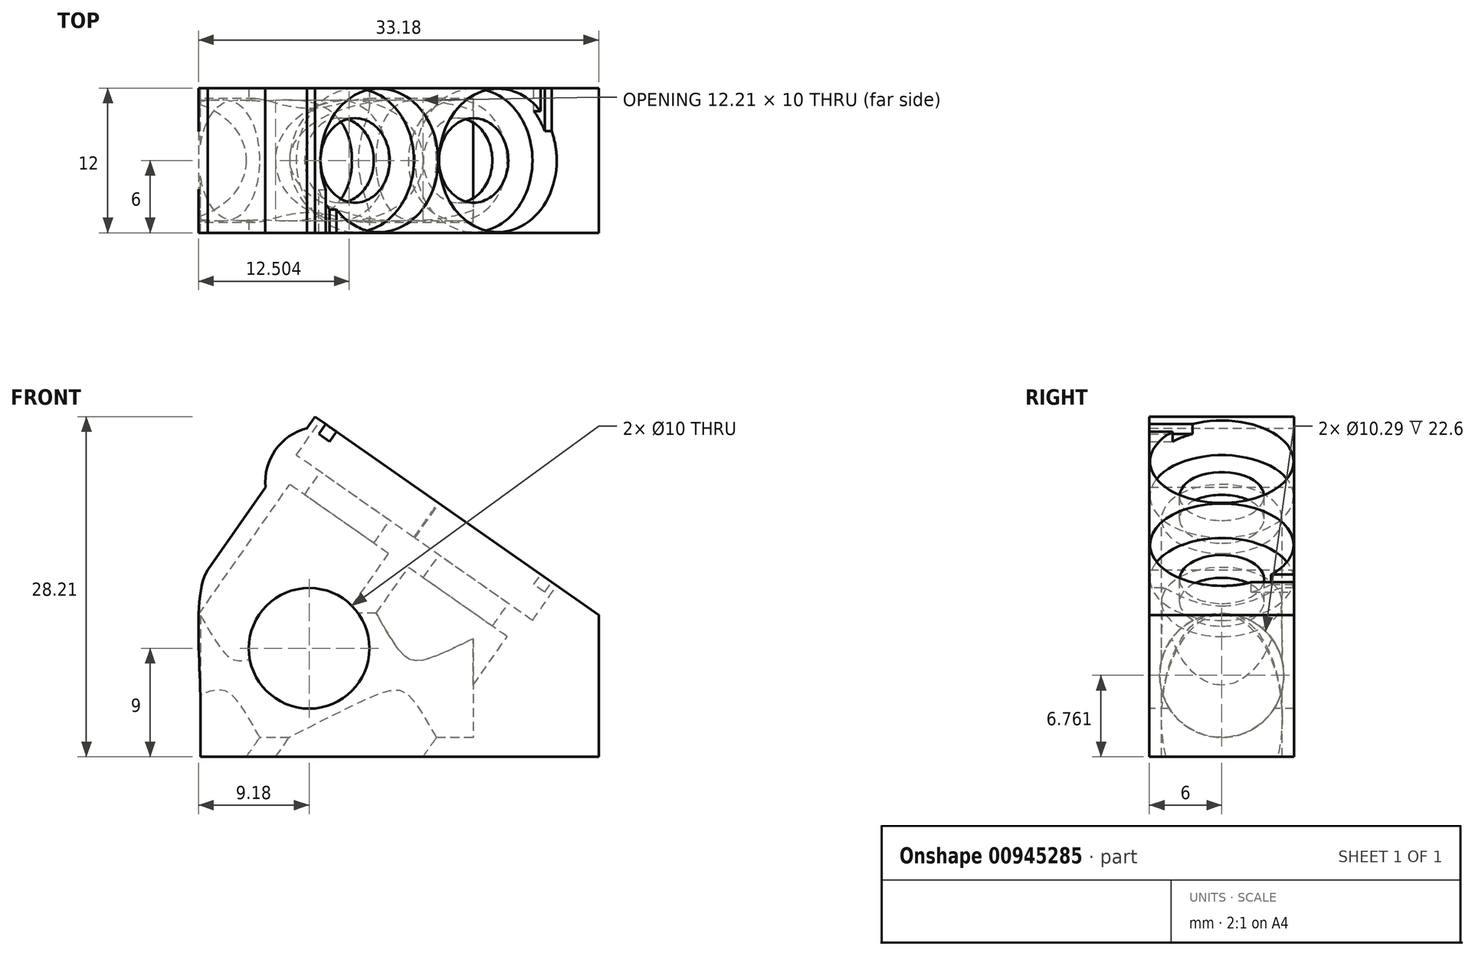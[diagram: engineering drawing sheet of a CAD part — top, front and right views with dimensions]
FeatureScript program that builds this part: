
annotation { "Feature Type Name" : "Feature", "Feature Type Description" : "" }
export const myFeature = defineFeature(function(context is Context, id is Id, definition is map)
    precondition{}
    {
        {
            var Q0;
            Q0=qCreatedBy(makeId("Front.planeOp"),FACE);
            var sketch = newSketch(context, id + "F0", { "sketchPlane" : qUnion([Q0])});
            skLineSegment(sketch, "E0.bottom", {"start": v(0, 0) * mm, "end": v(-33, 0) * mm});
            skLineSegment(sketch, "E0.top", {"start": v(0, 4) * mm, "end": v(-33, 4) * mm});
            skLineSegment(sketch, "E0.left", {"start": v(0, 0) * mm, "end": v(0, 4) * mm});
            skLineSegment(sketch, "E0.right", {"start": v(-33, 0) * mm, "end": v(-33, 4) * mm});
            skLineSegment(sketch, "E1", {"start": v(-30.88, 15.06) * mm, "end": v(-9.83, 0.32) * mm, "construction": true});
            skLineSegment(sketch, "E2", {"start": v(-9.83, 0.32) * mm, "end": v(-1.23, 12.6) * mm, "construction": true});
            skLineSegment(sketch, "E3", {"start": v(-1.23, 12.6) * mm, "end": v(0, 11.74) * mm, "construction": true});
            skLineSegment(sketch, "E4", {"start": v(-22.28, 27.35) * mm, "end": v(-30.88, 15.06) * mm, "construction": true});
            skLineSegment(sketch, "E5", {"start": v(0, 4) * mm, "end": v(0, 11.74) * mm});
            skLineSegment(sketch, "E6", {"start": v(-32.4, 15.5) * mm, "end": v(-15.96, 4) * mm});
            skLineSegment(sketch, "E7", {"start": v(0, 7.87) * mm, "end": v(13.32, 7.87) * mm});
            skLineSegment(sketch, "E8", {"start": v(13.32, 7.87) * mm, "end": v(13.32, 0) * mm});
            skLineSegment(sketch, "E9", {"start": v(13.32, 0) * mm, "end": v(0, 0) * mm});
            skLineSegment(sketch, "E10", {"start": v(21.82, 30.5) * mm, "end": v(-34.66, 30.5) * mm, "construction": true});
            skLineSegment(sketch, "E11", {"start": v(-22.28, 27.35) * mm, "end": v(-23.5, 28.2) * mm, "construction": true});
            skLineSegment(sketch, "E12", {"start": v(-23.5, 28.2) * mm, "end": v(-21.9, 30.5) * mm, "construction": true});
            skLineSegment(sketch, "E13", {"start": v(-21.9, 30.5) * mm, "end": v(1.6, 14.04) * mm, "construction": true});
            skLineSegment(sketch, "E14", {"start": v(0, 11.74) * mm, "end": v(1.6, 14.04) * mm, "construction": true});
            skLineSegment(sketch, "E15", {"start": v(-29.2, 13.88) * mm, "end": v(-31.73, 10.28) * mm, "construction": true});
            skLineSegment(sketch, "E16", {"start": v(-31.73, 10.28) * mm, "end": v(-14.04, -2.11) * mm, "construction": true});
            skLineSegment(sketch, "E17", {"start": v(-14.04, -2.11) * mm, "end": v(-11.51, 1.5) * mm, "construction": true});
            skLineSegment(sketch, "E18", {"start": v(-22.88, 4.08) * mm, "end": v(-20.36, 7.69) * mm, "construction": true});
            skLineSegment(sketch, "E19", {"start": v(0, 11.74) * mm, "end": v(-23.5, 28.2) * mm});
            skLineSegment(sketch, "E20", {"start": v(-23.5, 28.2) * mm, "end": v(-32.4, 15.5) * mm});
            skLineSegment(sketch, "E21", {"start": v(-1.1, 12.52) * mm, "end": v(-9.87, 0) * mm});
            skLineSegment(sketch, "E22", {"start": v(-22.4, 27.43) * mm, "end": v(-31.3, 14.74) * mm});
            skFitSpline(sketch, "E23", {"points": [v(-32.4, 15.5) * mm, v(-33, 4) * mm], "startDerivative": vector(-3.84, -5.87) * mm, "endDerivative": vector(0, -11.95) * mm});
            skLineSegment(sketch, "E24", {"start": v(-15.96, 4) * mm, "end": v(-10.25, 0) * mm});
            skLineSegment(sketch, "E25", {"start": v(-23.03, 26.54) * mm, "end": v(-25.92, 24.77) * mm});
            skLineSegment(sketch, "E26", {"start": v(-25.92, 24.77) * mm, "end": v(-26.47, 21.62) * mm});
            skLineSegment(sketch, "E27.MirrorCS", {"start": v(-1.73, 11.62) * mm, "end": v(-2.4, 8.3) * mm});
            skLineSegment(sketch, "E28.MirrorCS", {"start": v(-2.4, 8.3) * mm, "end": v(-5.17, 6.7) * mm});
            skArc(sketch, "E29", {"start": v(-24.18, 27.25) * mm, "mid": v(-26.8, 25.44) * mm, "end": v(-27.6, 22.35) * mm});
            skLineSegment(sketch, "E30", {"start": v(-23.25, 28.02) * mm, "end": v(-25.23, 25.19) * mm});
            skLineSegment(sketch, "E31.MirrorCS", {"start": v(-0.26, 11.93) * mm, "end": v(-2.25, 9.1) * mm});
            skSolve(sketch);
        }
        {
            var Q0;
            {var subQ0=sQuery(id+"F0.wireOp",EDGE,"E21");var subQ1=sQuery(id+"F0.wireOp",EDGE,"E19");var subQ2=makeQuery(id+"F0.imprint","INTERSECT",VERTEX,{"derivedFrom":[subQ1,subQ0]});Q0=makeQuery(id+"F0.imprint","IMPRINT",FACE,{"disambiguationData":[TD([[makeQuery(id+"F0.imprint","IMPRINT",EDGE,{"disambiguationData":[TD([[subQ2,-1.0]])],"derivedFrom":subQ1}),1.0]])]});}
            var Q1;
            {var subQ3=sQuery(id+"F0.wireOp",EDGE,"E26");Q1=makeQuery(id+"F0.imprint","IMPRINT",FACE,{"disambiguationData":[TD([[makeQuery(id+"F0.imprint","IMPRINT",EDGE,{"derivedFrom":subQ3}),1.0]])]});}
            var Q2;
            {var subQ4=sQuery(id+"F0.wireOp",EDGE,"E26");Q2=makeQuery(id+"F0.imprint","IMPRINT",FACE,{"disambiguationData":[TD([[makeQuery(id+"F0.imprint","IMPRINT",EDGE,{"derivedFrom":subQ4}),-1.0]])]});}
            var Q3;
            {var subQ2=sQuery(id+"F0.wireOp",EDGE,"E29");Q3=makeQuery(id+"F0.imprint","IMPRINT",FACE,{"disambiguationData":[TD([[makeQuery(id+"F0.imprint","IMPRINT",EDGE,{"derivedFrom":subQ2}),1.0]])]});}
            var Q4;
            {var subQ3=sQuery(id+"F0.wireOp",EDGE,"E30");Q4=makeQuery(id+"F0.imprint","IMPRINT",FACE,{"disambiguationData":[TD([[makeQuery(id+"F0.imprint","IMPRINT",EDGE,{"derivedFrom":subQ3}),1.0]])]});}
            var Q5;
            {var subQ6=sQuery(id+"F0.wireOp",EDGE,"E30");Q5=makeQuery(id+"F0.imprint","IMPRINT",FACE,{"disambiguationData":[TD([[makeQuery(id+"F0.imprint","IMPRINT",EDGE,{"derivedFrom":subQ6}),-1.0]])]});}
            var Q6;
            {var subQ0=sQuery(id+"F0.wireOp",EDGE,"E23");Q6=makeQuery(id+"F0.imprint","IMPRINT",FACE,{"disambiguationData":[TD([[makeQuery(id+"F0.imprint","IMPRINT",EDGE,{"derivedFrom":subQ0}),1.0]])]});}
            var Q7;
            {var subQ0=sQuery(id+"F0.wireOp",EDGE,"E0.right");Q7=makeQuery(id+"F0.imprint","IMPRINT",FACE,{"disambiguationData":[TD([[makeQuery(id+"F0.imprint","IMPRINT",EDGE,{"derivedFrom":subQ0}),-1.0]])]});}
            var Q8;
            {var subQ3=sQuery(id+"F0.wireOp",EDGE,"E24");Q8=makeQuery(id+"F0.imprint","IMPRINT",FACE,{"disambiguationData":[TD([[makeQuery(id+"F0.imprint","IMPRINT",EDGE,{"derivedFrom":subQ3}),1.0]])]});}
            var Q9;
            {var subQ0=sQuery(id+"F0.wireOp",EDGE,"E0.left");Q9=makeQuery(id+"F0.imprint","IMPRINT",FACE,{"disambiguationData":[TD([[makeQuery(id+"F0.imprint","IMPRINT",EDGE,{"derivedFrom":subQ0}),1.0]])]});}
            var Q10;
            {var subQ4=sQuery(id+"F0.wireOp",EDGE,"E28.MirrorCS");Q10=makeQuery(id+"F0.imprint","IMPRINT",FACE,{"disambiguationData":[TD([[makeQuery(id+"F0.imprint","IMPRINT",EDGE,{"derivedFrom":subQ4}),1.0]])]});}
            var Q11;
            {var subQ3=sQuery(id+"F0.wireOp",EDGE,"E28.MirrorCS");Q11=makeQuery(id+"F0.imprint","IMPRINT",FACE,{"disambiguationData":[TD([[makeQuery(id+"F0.imprint","IMPRINT",EDGE,{"derivedFrom":subQ3}),-1.0]])]});}
            var Q12;
            {var subQ3=sQuery(id+"F0.wireOp",EDGE,"E31.MirrorCS");Q12=makeQuery(id+"F0.imprint","IMPRINT",FACE,{"disambiguationData":[TD([[makeQuery(id+"F0.imprint","IMPRINT",EDGE,{"derivedFrom":subQ3}),-1.0]])]});}
            extrude(context, id + "F1", {"entities" : qUnion([Q0, Q1, Q2, Q3, Q4, Q5, Q6, Q7, Q8, Q9, Q10, Q11, Q12]), "endBound" : BoundingType.SYMMETRIC, "depth" : 12 * mm, "offsetDistance" : 25 * mm});
        }
        {
            var Q0;
            Q0=makeQuery(id+"F1.opExtrude","CAP_FACE",FACE,{"disambiguationData":[OSD([sQuery(id+"F0.wireOp",EDGE,"E0.bottom"),sQuery(id+"F0.wireOp",EDGE,"E0.left"),sQuery(id+"F0.wireOp",EDGE,"E0.right"),sQuery(id+"F0.wireOp",EDGE,"E5"),sQuery(id+"F0.wireOp",EDGE,"E19"),sQuery(id+"F0.wireOp",EDGE,"E20"),sQuery(id+"F0.wireOp",EDGE,"E23"),sQuery(id+"F0.wireOp",EDGE,"E29")])],"isStart":false});
            var sketch = newSketch(context, id + "F2", { "sketchPlane" : qUnion([Q0])});
            skCircle(sketch, "E32", {"center": v(-24, 9) * mm, "radius": 5 * mm});
            skSolve(sketch);
        }
        {
            var Q0;
            Q0=makeQuery(id+"F2.imprint","IMPRINT",FACE,{"disambiguationData":[TD([[makeQuery(id+"F2.imprint","IMPRINT",EDGE,{"derivedFrom":sQuery(id+"F2.wireOp",EDGE,"E32")}),1.0]])]});
            extrude(context, id + "F3", {"entities" : qUnion([Q0]), "operationType" : NewBodyOperationType.REMOVE, "oppositeDirection" : true, "depth" : 25 * mm, "offsetDistance" : 25 * mm});
        }
        {
            var Q0;
            Q0=makeQuery(id+"F1.opExtrude","SWEPT_FACE",FACE,{"disambiguationData":[OSD([sQuery(id+"F0.wireOp",EDGE,"E19")])]});
            var sketch = newSketch(context, id + "F4", { "sketchPlane" : qUnion([Q0])});
            skCircle(sketch, "E33", {"center": v(-28.94, 0) * mm, "radius": 3.5 * mm});
            skCircle(sketch, "E34", {"center": v(-16.94, 0) * mm, "radius": 3.5 * mm});
            skCircle(sketch, "E35", {"center": v(-28.94, 0) * mm, "radius": 5 * mm});
            skCircle(sketch, "E36", {"center": v(-16.94, 0) * mm, "radius": 5 * mm});
            skCircle(sketch, "E37", {"center": v(-28.94, 0) * mm, "radius": 5.95 * mm});
            skCircle(sketch, "E38", {"center": v(-16.94, 0) * mm, "radius": 5.95 * mm});
            skLineSegment(sketch, "E39", {"start": v(-34.37, -6) * mm, "end": v(-34.37, -2.43) * mm});
            skLineSegment(sketch, "E40", {"start": v(-33.27, -6) * mm, "end": v(-33.27, -4.08) * mm});
            skLineSegment(sketch, "E41", {"start": v(-12.6, 4.08) * mm, "end": v(-12.6, 6) * mm});
            skLineSegment(sketch, "E42", {"start": v(-11.5, 2.43) * mm, "end": v(-11.5, 6) * mm});
            skSolve(sketch);
        }
        {
            var Q0;
            Q0=makeQuery(id+"F4.imprint","IMPRINT",FACE,{"disambiguationData":[TD([[makeQuery(id+"F4.imprint","IMPRINT",EDGE,{"derivedFrom":sQuery(id+"F4.wireOp",EDGE,"E33")}),-1.0]])]});
            var Q1;
            Q1=makeQuery(id+"F4.imprint","IMPRINT",FACE,{"disambiguationData":[TD([[makeQuery(id+"F4.imprint","IMPRINT",EDGE,{"derivedFrom":sQuery(id+"F4.wireOp",EDGE,"E34")}),-1.0]])]});
            extrude(context, id + "F5", {"entities" : qUnion([Q0, Q1]), "operationType" : NewBodyOperationType.REMOVE, "oppositeDirection" : true, "depth" : 32.3 * mm, "offsetDistance" : 25 * mm, "hasSecondDirection" : true, "secondDirectionOppositeDirection" : true, "secondDirectionDepth" : 5.8 * mm});
        }
        {
            var Q0;
            Q0=makeQuery(id+"F4.imprint","IMPRINT",FACE,{"disambiguationData":[TD([[makeQuery(id+"F4.imprint","IMPRINT",EDGE,{"derivedFrom":sQuery(id+"F4.wireOp",EDGE,"E33")}),1.0]])]});
            var Q1;
            Q1=makeQuery(id+"F4.imprint","IMPRINT",FACE,{"disambiguationData":[TD([[makeQuery(id+"F4.imprint","IMPRINT",EDGE,{"derivedFrom":sQuery(id+"F4.wireOp",EDGE,"E34")}),1.0]])]});
            extrude(context, id + "F6", {"entities" : qUnion([Q0, Q1]), "operationType" : NewBodyOperationType.REMOVE, "oppositeDirection" : true, "depth" : 38.4 * mm, "offsetDistance" : 25 * mm});
        }
        {
            var Q0;
            Q0=makeQuery(id+"F4.imprint","IMPRINT",FACE,{"disambiguationData":[TD([[makeQuery(id+"F4.imprint","IMPRINT",EDGE,{"derivedFrom":sQuery(id+"F4.wireOp",EDGE,"E33")}),-1.0]])]});
            var Q1;
            Q1=makeQuery(id+"F4.imprint","IMPRINT",FACE,{"disambiguationData":[TD([[makeQuery(id+"F4.imprint","IMPRINT",EDGE,{"derivedFrom":sQuery(id+"F4.wireOp",EDGE,"E35")}),-1.0]])]});
            var Q2;
            Q2=makeQuery(id+"F4.imprint","IMPRINT",FACE,{"disambiguationData":[TD([[makeQuery(id+"F4.imprint","IMPRINT",EDGE,{"derivedFrom":sQuery(id+"F4.wireOp",EDGE,"E36")}),-1.0]])]});
            var Q3;
            Q3=makeQuery(id+"F4.imprint","IMPRINT",FACE,{"disambiguationData":[TD([[makeQuery(id+"F4.imprint","IMPRINT",EDGE,{"derivedFrom":sQuery(id+"F4.wireOp",EDGE,"E34")}),-1.0]])]});
            extrude(context, id + "F7", {"entities" : qUnion([Q0, Q1, Q2, Q3]), "operationType" : NewBodyOperationType.REMOVE, "oppositeDirection" : true, "depth" : 3.5 * mm, "offsetDistance" : 25 * mm});
        }
        {
            var Q0;
            {var subQ0=sQuery(id+"F0.wireOp",EDGE,"E0.bottom");var subQ1=sQuery(id+"F0.wireOp",EDGE,"E23");var subQ2=sQuery(id+"F0.wireOp",EDGE,"E0.right");Q0=makeQuery(id+"F5.boolean.opBoolean","SPLIT",FACE,{"disambiguationData":[TD([makeQuery(id+"F1.opExtrude","CAP_FACE",FACE,{"disambiguationData":[OSD([subQ0,sQuery(id+"F0.wireOp",EDGE,"E0.left"),subQ2,sQuery(id+"F0.wireOp",EDGE,"E5"),sQuery(id+"F0.wireOp",EDGE,"E19"),sQuery(id+"F0.wireOp",EDGE,"E20"),subQ1,sQuery(id+"F0.wireOp",EDGE,"E29")])],"isStart":false})])],"derivedFrom":makeQuery(id+"F1.opExtrude","SWEPT_FACE",FACE,{"disambiguationData":[OSD([subQ2])]})});}
            var sketch = newSketch(context, id + "F8", { "sketchPlane" : qUnion([Q0])});
            skCircle(sketch, "E43", {"center": v(0, 6.76) * mm, "radius": 5.15 * mm});
            skSolve(sketch);
        }
        {
            var Q0;
            Q0 = qSketchRegion(id + "F8", true);
            extrude(context, id + "F9", {"entities" : qUnion([Q0]), "operationType" : NewBodyOperationType.REMOVE, "oppositeDirection" : true, "depth" : 22.6 * mm, "offsetDistance" : 25 * mm});
        }
        {
            var Q0;
            {var subQ0=sQuery(id+"F4.wireOp",EDGE,"E39");Q0=makeQuery(id+"F4.imprint","IMPRINT",FACE,{"disambiguationData":[TD([[makeQuery(id+"F4.imprint","IMPRINT",EDGE,{"derivedFrom":subQ0}),-1.0]])]});}
            var Q1;
            {var subQ0=sQuery(id+"F4.wireOp",EDGE,"E41");Q1=makeQuery(id+"F4.imprint","IMPRINT",FACE,{"disambiguationData":[TD([[makeQuery(id+"F4.imprint","IMPRINT",EDGE,{"derivedFrom":subQ0}),-1.0]])]});}
            extrude(context, id + "F10", {"entities" : qUnion([Q0, Q1]), "operationType" : NewBodyOperationType.REMOVE, "oppositeDirection" : true, "depth" : 1 * mm, "offsetDistance" : 25 * mm});
        }
    });
